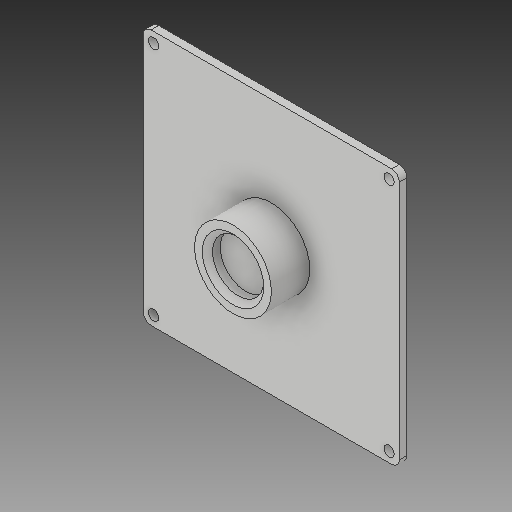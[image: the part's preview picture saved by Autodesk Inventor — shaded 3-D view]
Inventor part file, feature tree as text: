
AUTODESK INVENTOR PART (.ipt)
format: ipt  version: 2017 (Build 210142000, 142)  size: 142,848 bytes
history: native  units: mm
features: extrude x3, sketch x1, chamfer x1
ambient origin geometry x8: Origin, YZ Plane, XZ Plane, XY Plane, X Axis, Y Axis, Z Axis, Center Point
bodies: Solid1 (feature_tree)
feature tree (5):
  sketch  "Sketch1"  dims[d0=100.0mm d1=100.0mm d2=4.0mm d3=3.0mm d4=4.0mm d5=20.0mm d6=30.0mm d7=3.0mm d8=0.0mm d9=15.0mm d10=0.0mm d11=10.0mm d12=0.0mm d13=2.0mm d14=2.0mm d15=45.0deg]
  extrude  "Extrusion1"  Depth=100.0mm
  extrude  "Extrusion2"  Depth=2.0mm
  extrude  "Extrusion3"  Depth=3.0mm
  chamfer  "Chamfer1"  Distance=4.0mm
